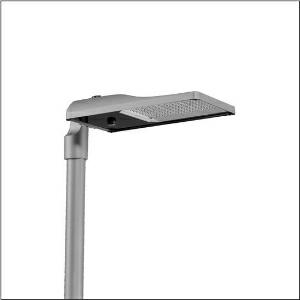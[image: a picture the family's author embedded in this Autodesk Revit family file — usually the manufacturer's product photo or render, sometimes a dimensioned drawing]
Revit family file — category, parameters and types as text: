
# Revit family: streetlight_sl_31_maxi___pl52_5xh8h31t08sa_1c4f
name_source: partatom
category: Lighting Fixtures
units: mm (PartAtom-declared; Revit-internal decimal feet)

## family parameters
Cut with Voids When Loaded = No
Host = Face
Light Source = No
Part Type = Normal
Room Calculation Point = No
Round Connector Dimension = Use Diameter
Shared = No

## types (1)
- --- (1 x LED, 27810 lm, 211.4 W, 3000K)
    Apparent Load = 211 VA
    CIE Flux Codes = 27 59 98 100 100
    Color Rendering = 70
    Color Temperature = 3000K
    Default Elevation = 1800 mm
    Description = Streetlight SL 31 maxi D4i, Desk-Remote mast luminaire for post-top, side-entry; light control with lens of PMMA; light distribution: PL52, direct asymmetric distribution, for standard-compliant lighting for roads and squares; LED: luminous flux: 27.810lm, light colour: 730, colour temperature: 3000K; luminous efficacy: 131,6lm/W; control: pre-setting: logarithmic dimming characteristic, flexible luminous flux parameterisation, time-dependent luminous flux control, constant luminous flux control, power reduction, intelligent temperature release in ECG and LED module, overheat protection; luminaire housing, of diecast aluminium, SITECO metallic grey (DB 702S), corrosivity category C5 high according to DIN EN ISO 12944; cover of toughened safety glass, transparent, opened without tools; mast flange of diecast aluminium, SITECO metallic grey (DB 702S), spigot size: 76/60mm, mast flange included unmounted; with cable H07RN-F 2x 1.5mm², cable length: 14,5m, connection cable pre-assembled; mains connection: 220..240V, AC, 50/60Hz; power consumption (at start of service life): 211,4W / (at end of service life): 238W / (with reduced operation 50%): 88,1W; protection rating (complete): IP66; insulation class (complete): insulation class II (safety insulation); impact resistance: IK09; certification: CE, ENEC, ENEC+, VDE, UKCA, ZD4i; permissible operating ambient temperature for outdoor applications: -40..+50°C; packaging unit: 1 piece

Light Distribution: PL52
    Height = 79 mm
    Lamp = 1 x LED
    Lamp Light Flux = 27810 lm
    Lamp Power = 211.4 W
    Lamp count = 1
    Length = 657 mm
    Luminous efficacy = 132 lm/W
    Manufacturer = Siteco
    ModVariant = No
    Model = 5XH8H31T08SA
    Number of Poles = 1
    OnlyDefault = Yes
    Power Factor = 1
    Product Name = Streetlight SL 31 maxi | PL52
    Product group = mast luminaire | pylon top
    ProductGroupID = 6100
    Protection Class = Protection class II
    Protection Degree = IP 66
    RLX_Detail_Level = 1
    RLX_Emergency_Light_Flux = 0 lm
    RLX_Emergency_Type = 0
    RLX_Emergency_Type_DB = No
    RlxData = <blob elided: 56833 chars, md5=66189649>
    Socket = socket
    Standby Power = 0 W
    System Light Flux = 27810 lm
    System Power = 211 W
    Type Comments = factory setting: luminous flux: 100 % | dim-lin: 254 | 727 mA
    Type Image = l_1300303.jpg
    URL = http://relux.com
    VarID = @adj_046979
    Voltage = 0 V
    Weight = 0.00 kg
    Width = 362 mm

## geometry (parser evidence)
native form markers: Blend x4, Sweep x11
no freeform markers — native parametric forms only
